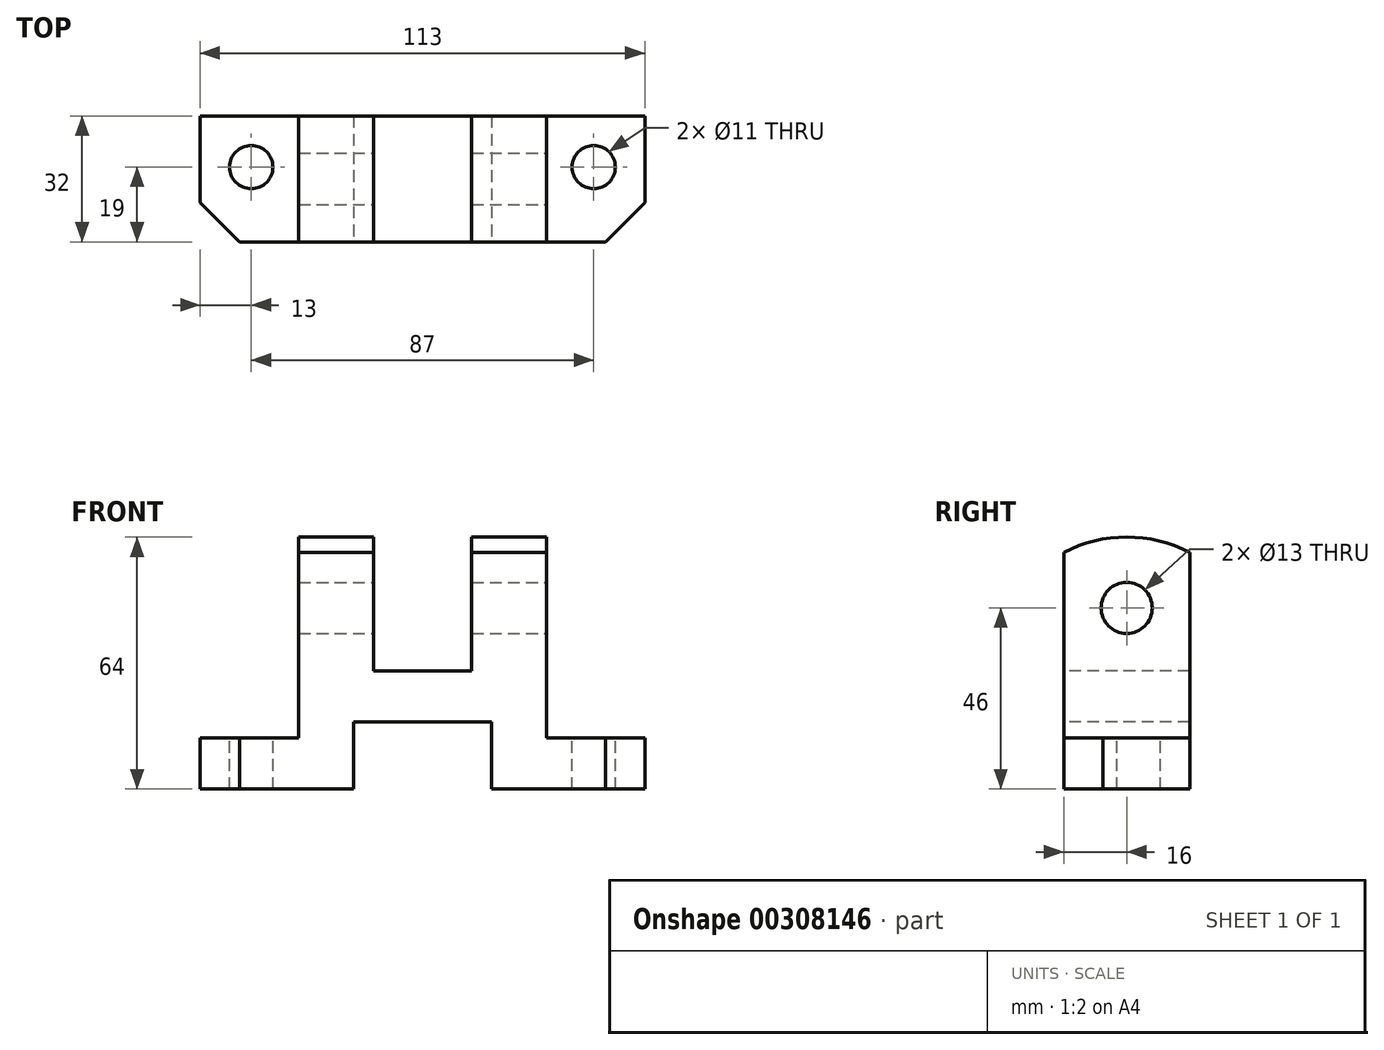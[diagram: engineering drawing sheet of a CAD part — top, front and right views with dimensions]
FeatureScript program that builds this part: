
annotation { "Feature Type Name" : "Feature", "Feature Type Description" : "" }
export const myFeature = defineFeature(function(context is Context, id is Id, definition is map)
    precondition{}
    {
        {
            var Q0;
            Q0=qCreatedBy(makeId("Front.planeOp"),FACE);
            var sketch = newSketch(context, id + "F0", { "sketchPlane" : qUnion([Q0])});
            skLineSegment(sketch, "E0", {"start": v(0, 0) * mm, "end": v(39, 0) * mm});
            skLineSegment(sketch, "E1", {"start": v(39, 0) * mm, "end": v(39, 17) * mm});
            skLineSegment(sketch, "E2", {"start": v(39, 17) * mm, "end": v(74, 17) * mm});
            skLineSegment(sketch, "E3", {"start": v(74, 17) * mm, "end": v(74, 0) * mm});
            skLineSegment(sketch, "E4", {"start": v(74, 0) * mm, "end": v(113, 0) * mm});
            skLineSegment(sketch, "E5", {"start": v(113, 0) * mm, "end": v(113, 13) * mm});
            skLineSegment(sketch, "E6", {"start": v(113, 13) * mm, "end": v(88, 13) * mm});
            skLineSegment(sketch, "E7", {"start": v(88, 13) * mm, "end": v(88, 30) * mm});
            skLineSegment(sketch, "E8", {"start": v(88, 30) * mm, "end": v(39, 30) * mm});
            skLineSegment(sketch, "E9", {"start": v(39, 30) * mm, "end": v(25, 30) * mm});
            skLineSegment(sketch, "E10", {"start": v(25, 30) * mm, "end": v(25, 13) * mm});
            skLineSegment(sketch, "E11", {"start": v(25, 13) * mm, "end": v(0, 13) * mm});
            skLineSegment(sketch, "E12", {"start": v(0, 13) * mm, "end": v(0, 0) * mm});
            skSolve(sketch);
        }
        {
            var Q0;
            Q0 = qSketchRegion(id + "F0", true);
            extrude(context, id + "F1", {"entities" : qUnion([Q0]), "oppositeDirection" : true, "depth" : 32 * mm});
        }
        {
            var Q0;
            Q0=makeQuery(id+"F1.opExtrude","SWEPT_FACE",FACE,{"disambiguationData":[OSD([sQuery(id+"F0.wireOp",EDGE,"E6")])]});
            var sketch = newSketch(context, id + "F2", { "sketchPlane" : qUnion([Q0])});
            skLineSegment(sketch, "E13", {"start": v(103, 0) * mm, "end": v(113, 0) * mm});
            skLineSegment(sketch, "E14", {"start": v(113, 0) * mm, "end": v(113, 10) * mm});
            skLineSegment(sketch, "E15", {"start": v(113, 10) * mm, "end": v(103, 0) * mm});
            skSolve(sketch);
        }
        {
            var Q0;
            Q0 = qSketchRegion(id + "F2", true);
            extrude(context, id + "F3", {"entities" : qUnion([Q0]), "operationType" : NewBodyOperationType.REMOVE, "oppositeDirection" : true, "depth" : 25 * mm});
        }
        {
            var Q0;
            Q0=makeQuery(id+"F1.opExtrude","SWEPT_FACE",FACE,{"disambiguationData":[OSD([sQuery(id+"F0.wireOp",EDGE,"E11")])]});
            var sketch = newSketch(context, id + "F4", { "sketchPlane" : qUnion([Q0])});
            skLineSegment(sketch, "E16", {"start": v(10, 0) * mm, "end": v(0, 10) * mm});
            skLineSegment(sketch, "E17", {"start": v(0, 10) * mm, "end": v(0, 0) * mm});
            skLineSegment(sketch, "E18", {"start": v(0, 0) * mm, "end": v(10, 0) * mm});
            skSolve(sketch);
        }
        {
            var Q0;
            Q0 = qSketchRegion(id + "F4", true);
            extrude(context, id + "F5", {"entities" : qUnion([Q0]), "operationType" : NewBodyOperationType.REMOVE, "oppositeDirection" : true, "depth" : 25 * mm});
        }
        {
            var Q0;
            Q0=makeQuery(id+"F1.opExtrude","SWEPT_FACE",FACE,{"disambiguationData":[OSD([sQuery(id+"F0.wireOp",EDGE,"E7")])]});
            var sketch = newSketch(context, id + "F6", { "sketchPlane" : qUnion([Q0])});
            skLineSegment(sketch, "E19", {"start": v(0, 30) * mm, "end": v(0, 60.13) * mm});
            skLineSegment(sketch, "E20", {"start": v(32, 30) * mm, "end": v(32, 60.13) * mm});
            skArc(sketch, "E21", {"start": v(32, 60.13) * mm, "mid": v(16, 64) * mm, "end": v(0, 60.13) * mm});
            skLineSegment(sketch, "E22", {"start": v(0, 30) * mm, "end": v(32, 30) * mm});
            skSolve(sketch);
        }
        {
            var Q0;
            Q0 = qSketchRegion(id + "F6", true);
            extrude(context, id + "F7", {"entities" : qUnion([Q0]), "operationType" : NewBodyOperationType.ADD, "oppositeDirection" : true, "depth" : 19 * mm});
        }
        {
            var Q0;
            Q0=makeQuery(id+"F1.opExtrude","SWEPT_FACE",FACE,{"disambiguationData":[OSD([sQuery(id+"F0.wireOp",EDGE,"E10")])]});
            var sketch = newSketch(context, id + "F8", { "sketchPlane" : qUnion([Q0])});
            skLineSegment(sketch, "E23", {"start": v(-32, 30) * mm, "end": v(-32, 60.13) * mm});
            skLineSegment(sketch, "E24", {"start": v(0, 30) * mm, "end": v(0, 60.13) * mm});
            skArc(sketch, "E25", {"start": v(0, 60.13) * mm, "mid": v(-16, 64) * mm, "end": v(-32, 60.13) * mm});
            skLineSegment(sketch, "E26", {"start": v(-32, 30) * mm, "end": v(0, 30) * mm});
            skSolve(sketch);
        }
        {
            var Q0;
            Q0 = qSketchRegion(id + "F8", true);
            extrude(context, id + "F9", {"entities" : qUnion([Q0]), "operationType" : NewBodyOperationType.ADD, "oppositeDirection" : true, "depth" : 19 * mm});
        }
        {
            var Q0;
            Q0=makeQuery(id+"F7.boolean.opBoolean","MERGE",FACE,{"derivedFrom":[makeQuery(id+"F1.opExtrude","SWEPT_FACE",FACE,{"disambiguationData":[OSD([sQuery(id+"F0.wireOp",EDGE,"E7")])]}),makeQuery(id+"F7.opExtrude","CAP_FACE",FACE,{"disambiguationData":[OSD([sQuery(id+"F6.wireOp",EDGE,"E19"),sQuery(id+"F6.wireOp",EDGE,"E20"),sQuery(id+"F6.wireOp",EDGE,"E21"),sQuery(id+"F6.wireOp",EDGE,"E22")])],"isStart":true})]});
            var sketch = newSketch(context, id + "F10", { "sketchPlane" : qUnion([Q0])});
            skCircle(sketch, "E27", {"center": v(16, 46) * mm, "radius": 6.5 * mm});
            skSolve(sketch);
        }
        {
            var Q0;
            Q0 = qSketchRegion(id + "F10", true);
            extrude(context, id + "F11", {"entities" : qUnion([Q0]), "operationType" : NewBodyOperationType.REMOVE, "oppositeDirection" : true, "depth" : 100 * mm});
        }
        {
            var Q0;
            Q0=makeQuery(id+"F1.opExtrude","SWEPT_FACE",FACE,{"disambiguationData":[OSD([sQuery(id+"F0.wireOp",EDGE,"E6")])]});
            var sketch = newSketch(context, id + "F12", { "sketchPlane" : qUnion([Q0])});
            skCircle(sketch, "E28", {"center": v(100, 19) * mm, "radius": 5.5 * mm});
            skSolve(sketch);
        }
        {
            var Q0;
            Q0 = qSketchRegion(id + "F12", true);
            extrude(context, id + "F13", {"entities" : qUnion([Q0]), "operationType" : NewBodyOperationType.REMOVE, "oppositeDirection" : true, "depth" : 25 * mm});
        }
        {
            var Q0;
            Q0=makeQuery(id+"F1.opExtrude","SWEPT_FACE",FACE,{"disambiguationData":[OSD([sQuery(id+"F0.wireOp",EDGE,"E11")])]});
            var sketch = newSketch(context, id + "F14", { "sketchPlane" : qUnion([Q0])});
            skCircle(sketch, "E29", {"center": v(13, 19) * mm, "radius": 5.5 * mm});
            skSolve(sketch);
        }
        {
            var Q0;
            Q0 = qSketchRegion(id + "F14", true);
            extrude(context, id + "F15", {"entities" : qUnion([Q0]), "operationType" : NewBodyOperationType.REMOVE, "oppositeDirection" : true, "depth" : 25 * mm});
        }
    });
